# Revit family: Indoor_Floor Lamp_Santa&Cole_TMM
name_source: partatom
category: Luminarias
revit_build: Autodesk Revit 2018 (Build: 20190510_1515(x64)
units: mm (PartAtom-declared; Revit-internal decimal feet)

## family parameters
Compartido = No
Corte con vacíos al cargar = No
Cota de conector redondo = Diámetro de uso
Número OmniClass = 23.80.70.00
Origen de luz = Sí
Punto de cálculo de habitación = No
Se basa en plano de trabajo = No
Siempre vertical = Sí
Tipo de pieza = Normal
Título OmniClass = Lighting

## types (3) — shared parameters
Cambio de temperatura de color de luz atenuada = <Ninguno>
Carga aparente = 12 VA
Fabricante = Santa & Cole
Filtro de color = 16777215
Load = 12 W
Lámpara = LED Bulb E26/E27
LED Bulb E26/E27
Manufacturer website = http://www.santacole.com
Modelo = TMM
Tamaño de símbolo de origen de luz = 50 mm  [stored 0.164042 ft]

## per-type parameters (varying)
| type | Assembly instructions - CE | Assembly instructions - UL | Code | Energy Label | Lamp Shade Material | Technical Information | URL | Upper Diffuser |
| Beige cardboard | http://www.santacole.com | http://www.santacole.com | TMMP1
TMMP1
TMMP1
TMMP1 | http://www.santacole.com | Santa & Cole - Beige Cardboard | http://www.santacole.com | http://www.santacole.com | No |
| White cardboard | http://www.santacole.com | http://www.santacole.com | TMMP2
TMMP2 | http://www.santacole.com | Santa & Cole - White Cardboard | http://www.santacole.com | http://www.santacole.com | No |
| White cardboard + Diffuser | https://www.santacole.com | https://www.santacole.com | TMMxx+TMMPx | https://www.santacole.com | Santa & Cole - White Cardboard | https://www.santacole.com | https://www.santacole.com | Sí |

note: [stored X ft] marks values corroborated as IEEE doubles in the binary element streams (Revit-internal decimal feet)

## geometry (parser evidence)
native form markers: Sweep x6
no freeform markers — native parametric forms only
